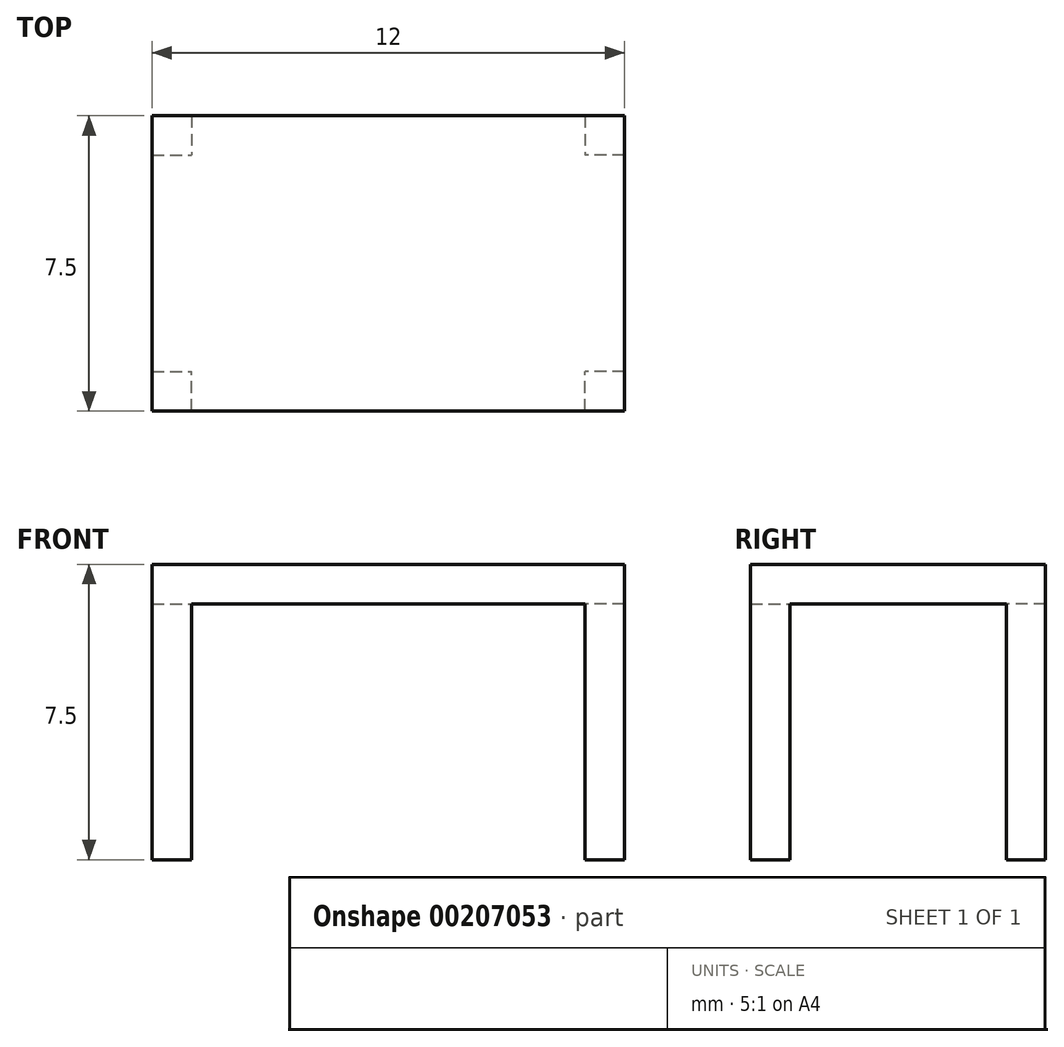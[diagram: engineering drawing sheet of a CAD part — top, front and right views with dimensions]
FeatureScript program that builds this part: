
annotation { "Feature Type Name" : "Feature", "Feature Type Description" : "" }
export const myFeature = defineFeature(function(context is Context, id is Id, definition is map)
    precondition{}
    {
        {
            var Q0;
            Q0=qCreatedBy(makeId("Top.planeOp"),FACE);
            var sketch = newSketch(context, id + "F0", { "sketchPlane" : qUnion([Q0])});
            skLineSegment(sketch, "E0.bottom", {"start": v(6, -3.75) * mm, "end": v(-6, -3.75) * mm});
            skLineSegment(sketch, "E0.top", {"start": v(6, 3.75) * mm, "end": v(-6, 3.75) * mm});
            skLineSegment(sketch, "E0.left", {"start": v(6, -3.75) * mm, "end": v(6, 3.75) * mm});
            skLineSegment(sketch, "E0.right", {"start": v(-6, -3.75) * mm, "end": v(-6, 3.75) * mm});
            skPoint(sketch, "E0.middle", {"position": v(0, 0) * mm});
            skSolve(sketch);
        }
        {
            var Q0;
            Q0=makeQuery(id+"F0.imprint","IMPRINT",FACE,{"disambiguationData":[TD([[makeQuery(id+"F0.imprint","IMPRINT",EDGE,{"derivedFrom":sQuery(id+"F0.wireOp",EDGE,"E0.bottom")}),-1.0]])]});
            extrude(context, id + "F1", {"entities" : qUnion([Q0]), "depth" : 1 * mm});
        }
        {
            var Q0;
            Q0=makeQuery(id+"F1.opExtrude","CAP_FACE",FACE,{"disambiguationData":[OSD([sQuery(id+"F0.wireOp",EDGE,"E0.bottom"),sQuery(id+"F0.wireOp",EDGE,"E0.top"),sQuery(id+"F0.wireOp",EDGE,"E0.left"),sQuery(id+"F0.wireOp",EDGE,"E0.right")])],"isStart":true});
            var sketch = newSketch(context, id + "F2", { "sketchPlane" : qUnion([Q0])});
            skLineSegment(sketch, "E1.bottom", {"start": v(6, 3.75) * mm, "end": v(5, 3.75) * mm});
            skLineSegment(sketch, "E1.top", {"start": v(6, 2.75) * mm, "end": v(5, 2.75) * mm});
            skLineSegment(sketch, "E1.left", {"start": v(6, 3.75) * mm, "end": v(6, 2.75) * mm});
            skLineSegment(sketch, "E1.right", {"start": v(5, 3.75) * mm, "end": v(5, 2.75) * mm});
            skLineSegment(sketch, "E2.bottom", {"start": v(-6, 3.75) * mm, "end": v(-5, 3.75) * mm});
            skLineSegment(sketch, "E2.top", {"start": v(-6, 2.75) * mm, "end": v(-5, 2.75) * mm});
            skLineSegment(sketch, "E2.left", {"start": v(-6, 3.75) * mm, "end": v(-6, 2.75) * mm});
            skLineSegment(sketch, "E2.right", {"start": v(-5, 3.75) * mm, "end": v(-5, 2.75) * mm});
            skLineSegment(sketch, "E3.bottom", {"start": v(-6, -3.75) * mm, "end": v(-5, -3.75) * mm});
            skLineSegment(sketch, "E3.top", {"start": v(-6, -2.75) * mm, "end": v(-5, -2.75) * mm});
            skLineSegment(sketch, "E3.left", {"start": v(-6, -3.75) * mm, "end": v(-6, -2.75) * mm});
            skLineSegment(sketch, "E3.right", {"start": v(-5, -3.75) * mm, "end": v(-5, -2.75) * mm});
            skLineSegment(sketch, "E4.bottom", {"start": v(6, -3.75) * mm, "end": v(5, -3.75) * mm});
            skLineSegment(sketch, "E4.top", {"start": v(6, -2.75) * mm, "end": v(5, -2.75) * mm});
            skLineSegment(sketch, "E4.left", {"start": v(6, -3.75) * mm, "end": v(6, -2.75) * mm});
            skLineSegment(sketch, "E4.right", {"start": v(5, -3.75) * mm, "end": v(5, -2.75) * mm});
            skSolve(sketch);
        }
        {
            var Q0;
            Q0=qSketchRegion(id+"F2",true);
            extrude(context, id + "F3", {"entities" : qUnion([Q0]), "operationType" : NewBodyOperationType.ADD, "depth" : 6.5 * mm});
        }
    });
